# Revit family: HeartFelt-Linear-Linear 40HL55_HunterDouglasEurope.LOG200
name_source: partatom
category: Specialty Equipment
revit_build: Autodesk Revit 2016 (Build: 20150220_1215(x64)
units: mm (PartAtom-declared; Revit-internal decimal feet)

## family parameters
Always vertical = No
Cut with Voids When Loaded = No
OmniClass Number = 23.35.70.24.11.17.14
OmniClass Title = Linear Ceilings
Part Type = Normal
Room Calculation Point = No
Round Connector Dimension = Use Diameter
Shared = No
Work Plane-Based = Yes

## types (10) — shared parameters
Article Code = 38.1201
BREEAM NL Credits = http://assets2.hunterdouglascontract.com
Ceiling System Data = http://assets2.hunterdouglascontract.com
Cradle-to-Cradle Bronze Certificate = http://assets2.hunterdouglascontract.com
Cradle-to-Cradle Material Health Certificate = http://assets2.hunterdouglascontract.com
Declaration of Performance = http://dop.hde.nl
Default Elevation = 1219.2 mm  [stored 4 ft]
EN 13964_Exposure Class = A, B
EN13501-1_Fire rating = Class B,s1,d0
GreenGuard Gold Certificate #410 = http://assets2.hunterdouglascontract.com
GreenGuard Gold Certificate #420 = http://assets2.hunterdouglascontract.com
Health and Hygiene Properties = http://assets2.hunterdouglascontract.com
Height = 55 mm  [stored 0.180446 ft]
Indoor Air Comfort Gold/ VOC Emission = http://assets2.hunterdouglascontract.com
Instalation Instructions = http://assets2.hunterdouglascontract.com
Instructions for Disassembly = http://assets2.hunterdouglascontract.com
LEED V4 Credits_EQ = Low-Emitting Materials, Indoor Air Quality Assessment, Acoustic Performance
LEED V4 Credits_MR = Building Product Disclosure
Maintenance Instructions = http://assets2.hunterdouglascontract.com
Manufacturer = Hunter Douglas
Material Safety Data Sheet = http://assets2.hunterdouglascontract.com
Model = HeartFelt Linear 40HL55
Oeko-Tex Standard 100 = http://assets2.hunterdouglascontract.com
Product Data = http://assets2.hunterdouglascontract.com
Product Line = HeartFelt® Linear
REACH Declaration = http://assets2.hunterdouglascontract.com
Sound Absorption Performance = http://assets2.hunterdouglascontract.com
Subcategory = HeartFelt® Ceilings
Substrate = Non-woven thermo-formable PES fibres
SundaHus Miljödata = http://assets2.hunterdouglascontract.com
Technical Specification = http://assets2.hunterdouglascontract.com
Thickness = 2.2 mm  [stored 0.00721785 ft]
URL = http://www.hunterdouglasarchitectural.eu
VOC class A+ Declaration = http://assets2.hunterdouglascontract.com
Width = 40 mm

## per-type parameters (varying)
| type | Colour Code | EN 410_Light reflectance_SOLAR | EN 410_Light reflectance_VIS | Material |
| 7575 Creme | 7575 | 46.7% | 39.4% | HeartFelt-7575-Creme_HunterDouglasEurope |
| 7576 Light Brown | 7576 | 33.8% | 28.3% | HeartFelt-7576-Light Brown_HunterDouglasEurope |
| 7577 Medium Brown | 7577 | 24.1% | 17.5% | HeartFelt-7577-Medium Brown_HunterDouglasEurope |
| 7578 Dark Brown | 7578 | 20.6% | 13.3% | HeartFelt-7578-Dark Brown_HunterDouglasEurope |
| 7579 Umber | 7579 | 15.7% | 9.5% | HeartFelt-7579-Umber_HunterDouglasEurope |
| 7593 White | 7593 | 59.7% | 60.7% | HeartFelt-7593-White_HunterDouglasEurope |
| 7594 Black | 7594 | 3.6% | 3.5% | HeartFelt-7594-Black_HunterDouglasEurope |
| 7596 Light Grey | 7596 | 32.2% | 31.8% | HeartFelt-7596-Light Grey_HunterDouglasEurope |
| 7597 Middle Grey | 7597 | 20.3% | 20.6% | HeartFelt-7597-Middle Grey_HunterDouglasEurope |
| 7598 Dark Grey | 7598 | 8.9% | 8.5% | HeartFelt-7598-Dark Grey_HunterDouglasEurope |

note: [stored X ft] marks values corroborated as IEEE doubles in the binary element streams (Revit-internal decimal feet)

## geometry (parser evidence)
native form markers: Sweep x1
no freeform markers — native parametric forms only
